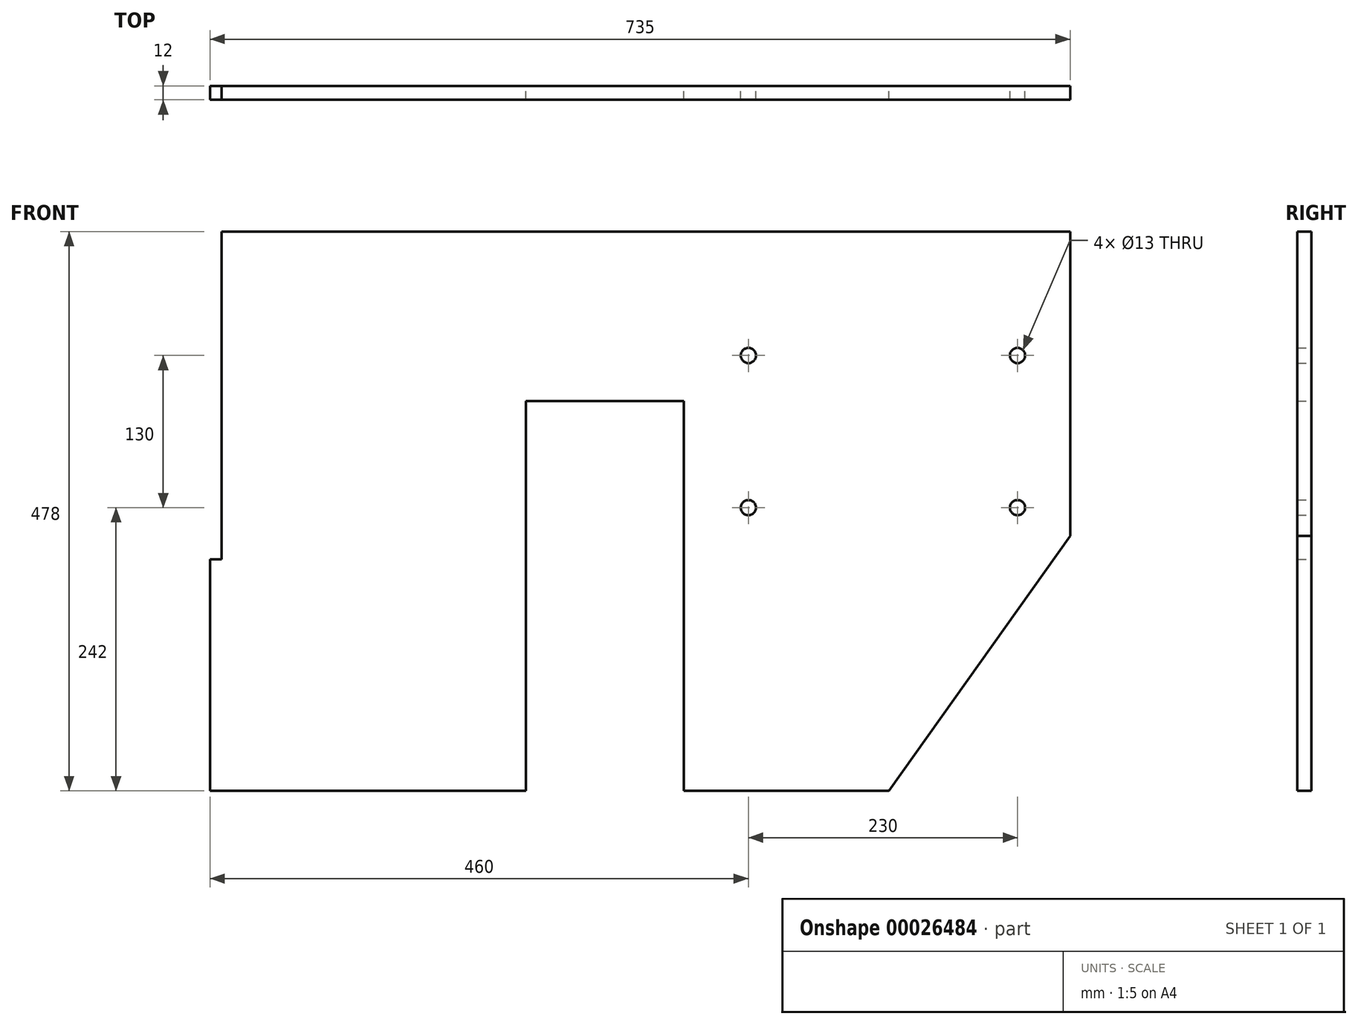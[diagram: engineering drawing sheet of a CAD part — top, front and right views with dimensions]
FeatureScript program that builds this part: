
annotation { "Feature Type Name" : "Feature", "Feature Type Description" : "" }
export const myFeature = defineFeature(function(context is Context, id is Id, definition is map)
    precondition{}
    {
        {
            var Q0;
            Q0=qCreatedBy(makeId("Front.planeOp"),FACE);
            var sketch = newSketch(context, id + "F0", { "sketchPlane" : qUnion([Q0])});
            skLineSegment(sketch, "E0", {"start": v(0, 0) * mm, "end": v(725, 0) * mm});
            skLineSegment(sketch, "E1", {"start": v(725, 0) * mm, "end": v(725, -260) * mm});
            skLineSegment(sketch, "E2", {"start": v(725, -260) * mm, "end": v(570, -478) * mm});
            skLineSegment(sketch, "E3", {"start": v(570, -478) * mm, "end": v(395, -478) * mm});
            skLineSegment(sketch, "E4", {"start": v(395, -478) * mm, "end": v(395, -145) * mm});
            skLineSegment(sketch, "E5", {"start": v(395, -145) * mm, "end": v(260, -145) * mm});
            skLineSegment(sketch, "E6", {"start": v(260, -145) * mm, "end": v(260, -478) * mm});
            skLineSegment(sketch, "E7", {"start": v(260, -478) * mm, "end": v(-10, -478) * mm});
            skLineSegment(sketch, "E8", {"start": v(-10, -478) * mm, "end": v(-10, -280) * mm});
            skLineSegment(sketch, "E9", {"start": v(-10, -280) * mm, "end": v(0, -280) * mm});
            skLineSegment(sketch, "E10", {"start": v(0, -280) * mm, "end": v(0, 0) * mm});
            skCircle(sketch, "E11", {"center": v(680, -106) * mm, "radius": 6.5 * mm});
            skCircle(sketch, "E12", {"center": v(680, -236) * mm, "radius": 6.5 * mm});
            skCircle(sketch, "E13", {"center": v(450, -236) * mm, "radius": 6.5 * mm});
            skCircle(sketch, "E14", {"center": v(450, -106) * mm, "radius": 6.5 * mm});
            skSolve(sketch);
        }
        {
            var Q0;
            Q0=makeQuery(id+"F0.imprint","IMPRINT",FACE,{"disambiguationData":[TD([[makeQuery(id+"F0.imprint","IMPRINT",EDGE,{"derivedFrom":sQuery(id+"F0.wireOp",EDGE,"E0")}),-1.0]])]});
            extrude(context, id + "F1", {"entities" : qUnion([Q0]), "depth" : 10 * mm});
        }
        {
            var Q0;
            Q0 = qSketchRegion(id + "F0", true);
            extrude(context, id + "F2", {"entities" : qUnion([Q0]), "operationType" : NewBodyOperationType.ADD, "depth" : 12 * mm});
        }
    });
